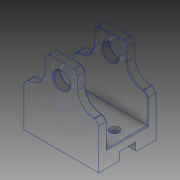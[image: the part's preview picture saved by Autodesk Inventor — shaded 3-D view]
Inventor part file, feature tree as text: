
AUTODESK INVENTOR PART (.ipt)
format: ipt  version: 2018.2 (Build 222227000, 227)  size: 320,512 bytes
history: native  units: mm
features: other x4, chamfer x4, sketch x4, extrude x3, hole x2, mirror x1
ambient origin geometry x8: Origin, YZ Plane, XZ Plane, XY Plane, X Axis, Y Axis, Z Axis, Center Point
bodies: Volumenkörper1 (feature_tree)
feature tree (18):
  other  "200-30-ROCKER-BOGIE-BEARING-01.ipt"
  extrude  "Grundkörper"  Depth=20.0mm
  extrude  "Ausschnitt"  Depth=70.0mm TaperAngle=0.0deg
  hole  "D20_Achsbohrung"  [1 undecoded]
  hole  "DIN7984_M6"  [1 undecoded]
  extrude  "Konturausschnitt"  Depth=10.0mm
  mirror  "Spiegeln1"
  chamfer  "Fase_Kontur"  Distance=5.0mm
  chamfer  "Fase_D20"  Distance=20.0mm
  chamfer  "Fase_Profil"  Distance=20.0mm
  chamfer  "Fase4"  Distance=10.0mm
  other  "Bezeichnung1"
  sketch  "Skizze1"  dims[d0=10.0mm d1=20.0mm]
  sketch  "Skizze3"  dims[d5=20.0mm d7=70.0mm d8=0.0mm]
  sketch  "Skizze4"  dims[d10=10.0mm d11=0.0mm]
  sketch  "Skizze5"  dims[d12=20.0mm d13=6.0mm d14=4.0mm d15=2.0mm d16=90.0deg d17=8.0mm d18=20.594885mm d20=25.0mm d22=20.0mm d23=10.0mm d24=5.0mm d25=20.0mm d27=30.0mm d28=20.0mm d30=30.0mm d33=6.6mm d34=6.0mm d35=11.0mm d36=4.4mm d37=90.0deg d38=8.0mm d39=20.594885mm d41=20.0mm d42=10.0mm d43=0.0mm d44=5.0mm d45=2.0mm d46=45.0deg d47=1.0mm d48=2.0mm d49=45.0deg d50=1.0mm d51=2.0mm d52=45.0deg d55=1.0mm d56=2.0mm d57=45.0deg]
  other  "Volumenkörper3::200-30-ROCKER-BOGIE-BEARING-01.ipt"
  other  "Flä1"
note: 2 required parameter values undecoded (feature->parameter linkage not recoverable at this tier; creation-order binding heuristic only, values carry confidence <= 0.55)
